# Revit family: HVAC_Water-Heaters_Enertech_CTC-EcoAir-622M
name_source: partatom
category: Specialty Equipment
revit_build: Autodesk Revit 2017 (Build: 20190508_0315(x64)
units: mm (PartAtom-declared; Revit-internal decimal feet)

## family parameters
Always vertical = Yes
Cut with Voids When Loaded = No
OmniClass Number = 23.75.00.00
OmniClass Title = Climate Control (HVAC)
Part Type = Normal
Room Calculation Point = No
Round Connector Dimension = Use Diameter
Shared = No
Work Plane-Based = No

## types (1)
- EcoAir 622M - 400V3N
    AirFlow = 4200 m3/h
    AssetType = Fixed
    BIMObjectName = HVAC_Water-Heaters_Enertech_CTC-EcoAir-622M
    Brand = CTC
    BrineSystem_Min_MaxPressure = 0.2 - 3.0 bar
    CO2Equivalent = 4.790 tonnes
    COP = 4.75
    Capacity = Variable
    Category = Heat Pumps, Air-to-water
    Color = grey
    ConvergoRefNr = 0091-1710-0001-SE
    Cost = 0 $
    Description = CTC EcoAir 600M, a series of speed controlled air-to-water heat pumps with an output of 2.5 to 22 kW, which automatically adapts to the building's power demand during the year. Models: 610M, 614M, 622M
    DurationUnit = Year
    EANNumber = 7333077087661
    EnergyClassHeatingWithControl = A+++ / A++
    EnergyClassHeatingWithoutControl = A++ / A++
    GroupFuse = 20 A
    HasProtectiveEarth = Yes
    IP_Code = IP X4
    IfcExportAs = IfcElectricalDeviceCommon
    IfcExportType = HEATER
    InPutPower = 2.19 kW
    Manufacturer = Enertech AB
    ManufacturerCountry = Sweden
    ManufacturerName = Enertech AB
    ManufacturerURL = https://ctc.se
    Material = Steel/copper
    MaxAirFlowRate = 5457 m3/h
    MaxOperatingPressureThermalStore = 3 bar
    MaxStartingCurrent = 4.9 A
    Model = CTC EcoAir 622M
    ModelNumber = 588401001
    NBSDescription = Air to water heat pumps
    NBSReference = 90-40-40/320
    Name = CTC-EcoAir-622M
    NominalCurrent = 0 A
    NominalDepth = 645 mm  [stored 2.11614 ft]
    NominalFrequencyRange = 50 Hz
    NominalHeight = 1180 mm  [stored 3.87139 ft]
    NominalVoltage = 400 V
    NominalWidth = 1375 mm  [stored 4.51115 ft]
    NumberOfPoles = 3
    OutputRange = 4.5-22 kW
    PhaseAngle = 0.00°
    PowerFactor = 0 W
    ProductInformation = CTC EcoAir 600M, a series of speed controlled air-to-water heat pumps with an output of 2.5 to 22 kW, which automatically adapts to the building's power demand during the year. Models: 610M, 614M, 622M
    PumpMainMaterial = Stainless Steel
    RatedCurrent = 17 A
    RatedHeatOutputModerate = 9 kW
    RatedVoltage = 1200 V
    RefrigerantQuantity = 2.7 kg
    RefrigerantType = R407C
    Revision = 3
    SCOPCold = 4.26
    SCOPModerate = 4.92
    SCOPWarm = 6.19
    Shape = Rectangular
    Size = 645x1375x1180 mm
    Sound pressureLPA 10m = 30 dB
    Sound pressureLPA 5m = 36 dB
    SoundPowerLWA = 55 dB
    SpecifiedOutput = 10.3 kW
    Touchscreen = no
    UNSPSCCode = 40101806
    URL = https://ctc-heating.com
    Uniclass2 = Pr_40_70_65
    Uniclass2015Description = Preparation catering equipment
    Uniclass2015Reference = Pr_40_70_65
    UsageCurrent = 0 A
    Version = 1
    VersionDate = 01/07/2019
    WarrantyDurationUnit = Year
    WaterVolumeHeathingSystem = 2.8 liters
    Weight = 192 kg

note: [stored X ft] marks values corroborated as IEEE doubles in the binary element streams (Revit-internal decimal feet)

## geometry (parser evidence)
native form markers: Sweep x3
no freeform markers — native parametric forms only
